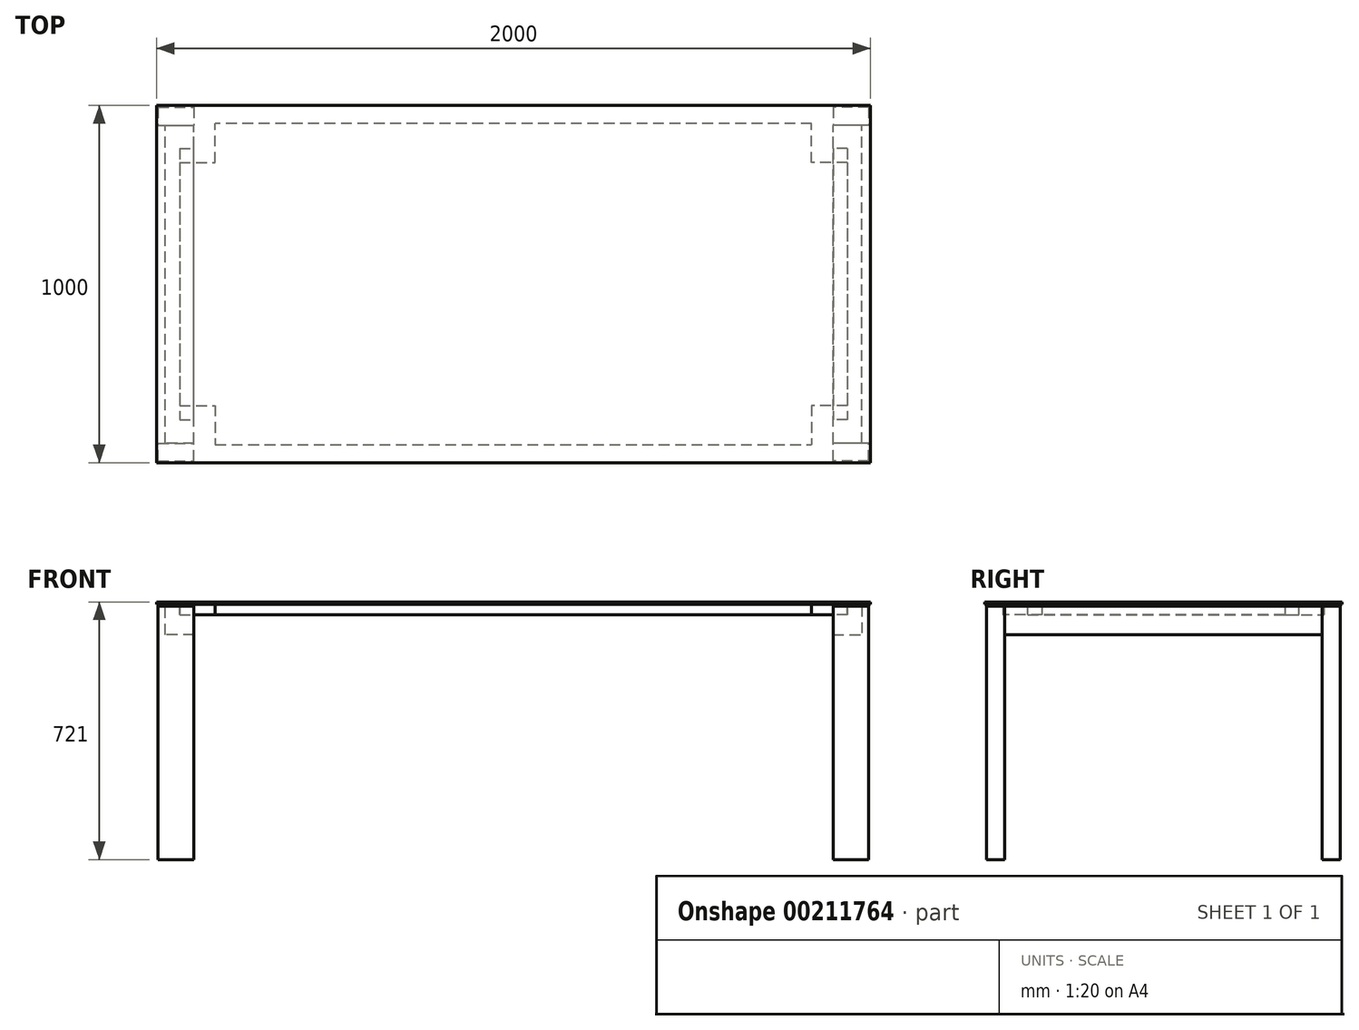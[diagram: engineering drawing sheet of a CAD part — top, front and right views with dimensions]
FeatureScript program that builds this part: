
annotation { "Feature Type Name" : "Feature", "Feature Type Description" : "" }
export const myFeature = defineFeature(function(context is Context, id is Id, definition is map)
    precondition{}
    {
        {
            var Q0;
            Q0=qCreatedBy(makeId("Top.planeOp"),FACE);
            var sketch = newSketch(context, id + "F0", { "sketchPlane" : qUnion([Q0])});
            skLineSegment(sketch, "E0.bottom", {"start": v(-995, 495) * mm, "end": v(-895, 495) * mm});
            skLineSegment(sketch, "E0.top", {"start": v(-995, 445) * mm, "end": v(-895, 445) * mm});
            skLineSegment(sketch, "E0.left", {"start": v(-995, 495) * mm, "end": v(-995, 445) * mm});
            skLineSegment(sketch, "E0.right", {"start": v(-895, 495) * mm, "end": v(-895, 445) * mm});
            skLineSegment(sketch, "E1.MirrorCS", {"start": v(995, 495) * mm, "end": v(995, 445) * mm});
            skLineSegment(sketch, "E2.MirrorCS", {"start": v(895, 495) * mm, "end": v(895, 445) * mm});
            skLineSegment(sketch, "E3.MirrorCS", {"start": v(995, 495) * mm, "end": v(895, 495) * mm});
            skLineSegment(sketch, "E4.MirrorCS", {"start": v(995, 445) * mm, "end": v(895, 445) * mm});
            skLineSegment(sketch, "E5.MirrorCS", {"start": v(895, -495) * mm, "end": v(895, -445) * mm});
            skLineSegment(sketch, "E6.MirrorCS", {"start": v(995, -495) * mm, "end": v(995, -445) * mm});
            skLineSegment(sketch, "E7.MirrorCS", {"start": v(-895, -495) * mm, "end": v(-895, -445) * mm});
            skLineSegment(sketch, "E8.MirrorCS", {"start": v(-995, -495) * mm, "end": v(-995, -445) * mm});
            skLineSegment(sketch, "E9.MirrorCS", {"start": v(-995, -495) * mm, "end": v(-895, -495) * mm});
            skLineSegment(sketch, "E10.MirrorCS", {"start": v(995, -495) * mm, "end": v(895, -495) * mm});
            skLineSegment(sketch, "E11.MirrorCS", {"start": v(995, -445) * mm, "end": v(895, -445) * mm});
            skLineSegment(sketch, "E12.MirrorCS", {"start": v(-995, -445) * mm, "end": v(-895, -445) * mm});
            skSolve(sketch);
        }
        {
            var Q0;
            Q0 = qSketchRegion(id + "F0", true);
            extrude(context, id + "F1", {"entities" : qUnion([Q0]), "depth" : 710 * mm});
        }
        {
            var Q0;
            Q0=makeQuery(id+"F1.opExtrude","SWEPT_FACE",FACE,{"disambiguationData":[OSD([sQuery(id+"F0.wireOp",EDGE,"E0.top")])]});
            var sketch = newSketch(context, id + "F2", { "sketchPlane" : qUnion([Q0])});
            skLineSegment(sketch, "E13.bottom", {"start": v(-975, 710) * mm, "end": v(-895, 710) * mm});
            skLineSegment(sketch, "E13.top", {"start": v(-975, 630) * mm, "end": v(-895, 630) * mm});
            skLineSegment(sketch, "E13.left", {"start": v(-975, 710) * mm, "end": v(-975, 630) * mm});
            skLineSegment(sketch, "E13.right", {"start": v(-895, 710) * mm, "end": v(-895, 630) * mm});
            skLineSegment(sketch, "E14.0", {"start": v(895, 710) * mm, "end": v(895, 630) * mm});
            skLineSegment(sketch, "E15.0", {"start": v(975, 710) * mm, "end": v(895, 710) * mm});
            skLineSegment(sketch, "E16.0", {"start": v(975, 710) * mm, "end": v(975, 630) * mm});
            skLineSegment(sketch, "E17", {"start": v(895, 630) * mm, "end": v(975, 630) * mm});
            skPoint(sketch, "E18.orphan", {"position": v(895, 0) * mm});
            skPoint(sketch, "E19.orphan", {"position": v(995, 0) * mm});
            skPoint(sketch, "E20.orphan", {"position": v(995, 710) * mm});
            skSolve(sketch);
        }
        {
            var Q0;
            Q0 = qSketchRegion(id + "F2", true);
            extrude(context, id + "F3", {"entities" : qUnion([Q0]), "endBound" : BoundingType.UP_TO_NEXT, "depth" : 25 * mm});
        }
        {
            var Q0;
            Q0=makeQuery(id+"F3.opExtrude","SWEPT_FACE",FACE,{"disambiguationData":[OSD([sQuery(id+"F2.wireOp",EDGE,"E13.bottom")])]});
            var sketch = newSketch(context, id + "F4", { "sketchPlane" : qUnion([Q0])});
            skLineSegment(sketch, "E21", {"start": v(-975, 0) * mm, "end": v(975, 0) * mm, "construction": true});
            skPoint(sketch, "E21.endSnap0", {"position": v(-975, 0) * mm});
            skLineSegment(sketch, "E22", {"start": v(-935, 0) * mm, "end": v(-935, -380) * mm});
            skLineSegment(sketch, "E23", {"start": v(-935, -380) * mm, "end": v(-895, -380) * mm});
            skLineSegment(sketch, "E24", {"start": v(-895, -380) * mm, "end": v(-895, 0) * mm});
            skLineSegment(sketch, "E25.MirrorCS", {"start": v(-935, 380) * mm, "end": v(-895, 380) * mm});
            skLineSegment(sketch, "E26.MirrorCS", {"start": v(-935, 0) * mm, "end": v(-935, 380) * mm});
            skLineSegment(sketch, "E27.MirrorCS", {"start": v(-895, 380) * mm, "end": v(-895, 0) * mm});
            skLineSegment(sketch, "E28.MirrorCS", {"start": v(935, 380) * mm, "end": v(895, 380) * mm});
            skLineSegment(sketch, "E29.MirrorCS", {"start": v(935, -380) * mm, "end": v(895, -380) * mm});
            skLineSegment(sketch, "E30.MirrorCS", {"start": v(895, 380) * mm, "end": v(895, 0) * mm});
            skLineSegment(sketch, "E31.MirrorCS", {"start": v(935, 0) * mm, "end": v(935, 380) * mm});
            skLineSegment(sketch, "E32.MirrorCS", {"start": v(935, 0) * mm, "end": v(935, -380) * mm});
            skLineSegment(sketch, "E33.MirrorCS", {"start": v(895, -380) * mm, "end": v(895, 0) * mm});
            skSolve(sketch);
        }
        {
            var Q0;
            Q0 = qSketchRegion(id + "F4", true);
            extrude(context, id + "F5", {"entities" : qUnion([Q0]), "operationType" : NewBodyOperationType.REMOVE, "oppositeDirection" : true, "depth" : 25 * mm});
        }
        {
            var Q0;
            Q0=makeQuery(id+"F5.boolean.opBoolean","COPY",FACE,{"derivedFrom":makeQuery(id+"F5.opExtrude","CAP_FACE",FACE,{"disambiguationData":[OSD([sQuery(id+"F4.wireOp",EDGE,"E22"),sQuery(id+"F4.wireOp",EDGE,"E23"),sQuery(id+"F4.wireOp",EDGE,"E24"),sQuery(id+"F4.wireOp",EDGE,"E25.MirrorCS"),sQuery(id+"F4.wireOp",EDGE,"E26.MirrorCS"),sQuery(id+"F4.wireOp",EDGE,"E27.MirrorCS")])],"isStart":false})});
            var sketch = newSketch(context, id + "F6", { "sketchPlane" : qUnion([Q0])});
            skLineSegment(sketch, "E34", {"start": v(-935, 0) * mm, "end": v(-935, -340) * mm});
            skLineSegment(sketch, "E35", {"start": v(-935, -340) * mm, "end": v(-835, -340) * mm});
            skLineSegment(sketch, "E36", {"start": v(-835, -340) * mm, "end": v(-835, -450) * mm});
            skLineSegment(sketch, "E37", {"start": v(-835, -450) * mm, "end": v(0, -450) * mm});
            skLineSegment(sketch, "E38.MirrorCS", {"start": v(-835, 450) * mm, "end": v(0, 450) * mm});
            skLineSegment(sketch, "E39.MirrorCS", {"start": v(-835, 340) * mm, "end": v(-835, 450) * mm});
            skLineSegment(sketch, "E40.MirrorCS", {"start": v(-935, 340) * mm, "end": v(-835, 340) * mm});
            skLineSegment(sketch, "E41.MirrorCS", {"start": v(-935, 0) * mm, "end": v(-935, 340) * mm});
            skLineSegment(sketch, "E42.MirrorCS", {"start": v(835, -340) * mm, "end": v(835, -450) * mm});
            skLineSegment(sketch, "E43.MirrorCS", {"start": v(835, 450) * mm, "end": v(0, 450) * mm});
            skLineSegment(sketch, "E44.MirrorCS", {"start": v(935, 0) * mm, "end": v(935, -340) * mm});
            skLineSegment(sketch, "E45.MirrorCS", {"start": v(935, 0) * mm, "end": v(935, 340) * mm});
            skLineSegment(sketch, "E46.MirrorCS", {"start": v(835, -450) * mm, "end": v(0, -450) * mm});
            skLineSegment(sketch, "E47.MirrorCS", {"start": v(835, 340) * mm, "end": v(835, 450) * mm});
            skLineSegment(sketch, "E48.MirrorCS", {"start": v(935, -340) * mm, "end": v(835, -340) * mm});
            skLineSegment(sketch, "E49.MirrorCS", {"start": v(935, 340) * mm, "end": v(835, 340) * mm});
            skSolve(sketch);
        }
        {
            var Q0;
            Q0 = qSketchRegion(id + "F6", true);
            extrude(context, id + "F7", {"entities" : qUnion([Q0]), "depth" : 30 * mm});
        }
        {
            var Q0;
            Q0=makeQuery(id+"F7.opExtrude","CAP_FACE",FACE,{"disambiguationData":[OSD([sQuery(id+"F6.wireOp",EDGE,"E34"),sQuery(id+"F6.wireOp",EDGE,"E35"),sQuery(id+"F6.wireOp",EDGE,"E36"),sQuery(id+"F6.wireOp",EDGE,"E37"),sQuery(id+"F6.wireOp",EDGE,"E38.MirrorCS"),sQuery(id+"F6.wireOp",EDGE,"E39.MirrorCS"),sQuery(id+"F6.wireOp",EDGE,"E40.MirrorCS"),sQuery(id+"F6.wireOp",EDGE,"E41.MirrorCS"),sQuery(id+"F6.wireOp",EDGE,"E42.MirrorCS"),sQuery(id+"F6.wireOp",EDGE,"E43.MirrorCS"),sQuery(id+"F6.wireOp",EDGE,"E44.MirrorCS"),sQuery(id+"F6.wireOp",EDGE,"E45.MirrorCS"),sQuery(id+"F6.wireOp",EDGE,"E46.MirrorCS"),sQuery(id+"F6.wireOp",EDGE,"E47.MirrorCS"),sQuery(id+"F6.wireOp",EDGE,"E48.MirrorCS"),sQuery(id+"F6.wireOp",EDGE,"E49.MirrorCS")])],"isStart":false});
            var sketch = newSketch(context, id + "F8", { "sketchPlane" : qUnion([Q0])});
            skLineSegment(sketch, "E50.bottom", {"start": v(1000, -500) * mm, "end": v(-1000, -500) * mm});
            skLineSegment(sketch, "E50.top", {"start": v(1000, 500) * mm, "end": v(-1000, 500) * mm});
            skLineSegment(sketch, "E50.left", {"start": v(1000, -500) * mm, "end": v(1000, 500) * mm});
            skLineSegment(sketch, "E50.right", {"start": v(-1000, -500) * mm, "end": v(-1000, 500) * mm});
            skPoint(sketch, "E50.middle", {"position": v(0, 0) * mm});
            skSolve(sketch);
        }
        {
            var Q0;
            Q0 = qSketchRegion(id + "F8", true);
            extrude(context, id + "F9", {"entities" : qUnion([Q0]), "depth" : 6 * mm});
        }
    });
